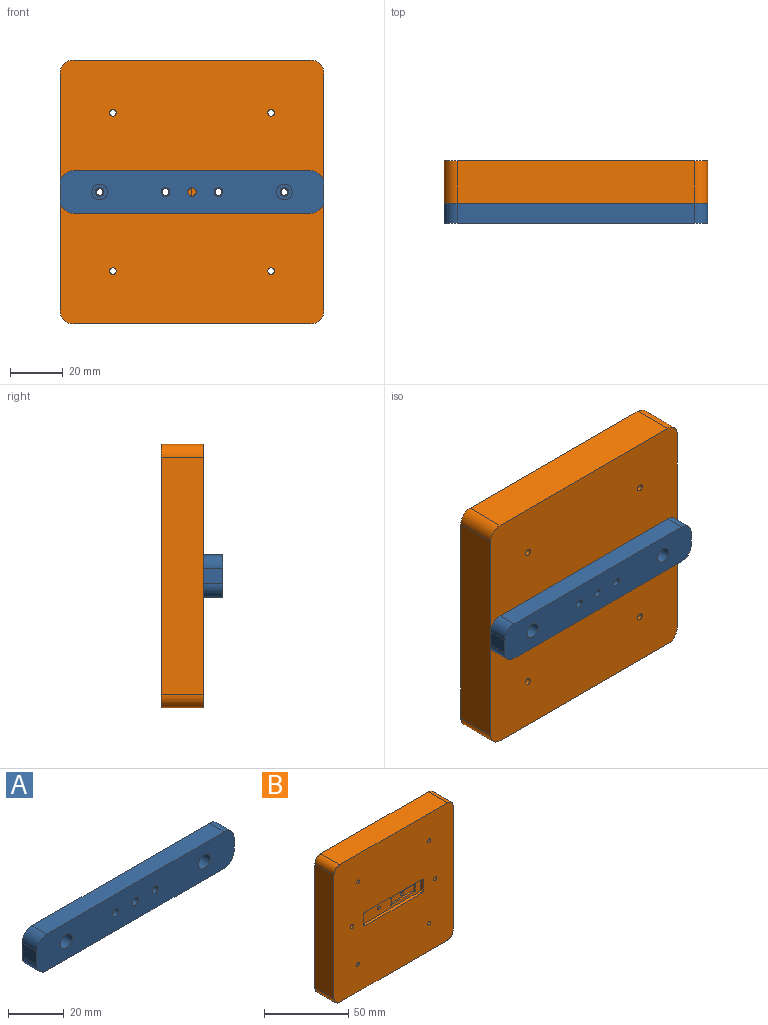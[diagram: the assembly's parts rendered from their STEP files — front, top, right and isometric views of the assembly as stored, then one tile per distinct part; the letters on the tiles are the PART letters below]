
ASSEMBLY  parts=2 mates=1
PART A: 40 faces, bbox 100x7.5x16 mm
  f0: cylinder r=1.6mm len=7mm, axis (0,-1,0), area 65mm2, adj f3,f18,f38
  f1: plane 90x7.5mm, normal (0,0,-1), area 660.3mm2, adj f3,f4,f32,f33,f34,f37,f38
  f2: cylinder r=1.6mm len=5.9mm, axis (0,-1,0), area 53.9mm2, adj f3,f27,f32
  f3: plane 100x16mm, normal (0,-1,0), area 1497.9mm2, adj f0,f1,f2,f5,f6,f7,f10,f12
  f4: plane 100x16mm, normal (0,1,0), area 1064.4mm2, adj f1,f5,f6,f7,f8,f9,f14,f15
  f5: plane 7.5x6mm, normal (1,0,0), area 45mm2, adj f3,f4,f34,f35
  f6: plane 90x7.5mm, normal (0,0,1), area 675mm2, adj f3,f4,f35,f36
  f7: plane 7.5x6mm, normal (-1,0,0), area 45mm2, adj f3,f4,f36,f37
  f8: cylinder r=1.6mm len=3.2mm, axis (0,-1,0), area 31.2mm2, adj f4,f13
  f9: cylinder r=1.6mm len=3.2mm, axis (0,-1,0), area 31.2mm2, adj f4,f11
  f10: cylinder r=3mm len=6mm, axis (0,-1,0), area 82.9mm2, adj f3,f11
  f11: plane 6x6mm, normal (0,-1,0), area 20.2mm2, adj f9,f10
  f12: cylinder r=3mm len=6mm, axis (0,-1,0), area 82.9mm2, adj f3,f13
  f13: plane 6x6mm, normal (0,-1,0), area 20.2mm2, adj f8,f12
  f14: plane 7x0.5mm, normal (1,0,0), area 3.5mm2, adj f4,f18,f28,f31
  f15: plane 47x0.5mm, normal (0,0,-1), area 23.5mm2, adj f4,f18,f28,f29
  f16: plane 7x0.5mm, normal (-1,0,0), area 3.5mm2, adj f4,f18,f29,f30
  f17: plane 47x0.5mm, normal (0,0,1), area 23.5mm2, adj f4,f18,f30,f31
  f18: plane 50x10mm, normal (0,1,0), area 382.6mm2, adj f0,f14,f15,f16,f17,f19,f20,f21
  f19: plane 19.2x1.1mm, normal (0,0,1), area 21.1mm2, adj f18,f20,f26,f27
  f20: cylinder r=0.5mm len=1.1mm, axis (0,1,0), area 2.6mm2, adj f18,f19,f21,f27
  f21: plane 4.2x1.1mm, normal (1,0,0), area 4.6mm2, adj f18,f20,f22,f27
  f22: cylinder r=0.5mm len=1.1mm, axis (0,1,0), area 2.6mm2, adj f18,f21,f23,f27
  f23: plane 19.2x1.1mm, normal (0,0,-1), area 21.1mm2, adj f18,f22,f24,f27
  f24: cylinder r=0.5mm len=1.1mm, axis (0,1,0), area 2.6mm2, adj f18,f23,f25,f27
  f25: plane 4.2x1.1mm, normal (-1,0,0), area 4.6mm2, adj f18,f24,f26,f27
  f26: cylinder r=0.5mm len=1.1mm, axis (0,1,0), area 2.6mm2, adj f18,f19,f25,f27
  f27: plane 21.2x6.2mm, normal (0,1,0), area 91.3mm2, adj f2,f19,f20,f21,f22,f23,f24,f25
  f28: cylinder r=1.5mm len=1.5mm, axis (0,-1,0), area 1.2mm2, adj f4,f14,f15,f18
  f29: cylinder r=1.5mm len=1.5mm, axis (0,1,0), area 1.2mm2, adj f4,f15,f16,f18
  f30: cylinder r=1.5mm len=1.5mm, axis (0,-1,0), area 1.2mm2, adj f4,f16,f17,f18
  f31: cylinder r=1.5mm len=1.5mm, axis (0,1,0), area 1.2mm2, adj f4,f14,f17,f18
  f32: cylinder r=1.25mm len=7mm, axis (0,0,-1), area 52.5mm2, adj f1,f2
  f33: cylinder r=1.25mm len=7mm, axis (0,0,-1), area 52.5mm2, adj f1,f39
  f34: cylinder r=5mm len=7.5mm, axis (0,1,0), area 58.9mm2, adj f1,f3,f4,f5
  f35: cylinder r=5mm len=7.5mm, axis (0,-1,0), area 58.9mm2, adj f3,f4,f5,f6
  f36: cylinder r=5mm len=7.5mm, axis (0,1,0), area 58.9mm2, adj f3,f4,f6,f7
  f37: cylinder r=5mm len=7.5mm, axis (0,-1,0), area 58.9mm2, adj f1,f3,f4,f7
  f38: cylinder r=1.25mm len=7mm, axis (0,0,-1), area 52.5mm2, adj f0,f1
  f39: cylinder r=1.6mm len=5.9mm, axis (0,-1,0), area 53.9mm2, adj f3,f27,f33
PART B: 49 faces, bbox 100x16x100 mm
  f0: plane 50x10mm, normal (0,-1,0), area 385.4mm2, adj f12,f13,f14,f15,f34,f35,f36,f37
  f1: plane 100x100mm, normal (0,-1,0), area 9451mm2, adj f3,f4,f5,f6,f12,f13,f14,f15
  f2: plane 100x100mm, normal (0,1,0), area 8151mm2, adj f3,f4,f5,f6,f7,f8,f9,f10
  f3: plane 90x16mm, normal (1,0,0), area 1440mm2, adj f1,f2,f26,f29
  f4: plane 90x16mm, normal (0,0,1), area 1440mm2, adj f1,f2,f26,f27
  f5: plane 90x16mm, normal (-1,0,0), area 1440mm2, adj f1,f2,f27,f28
  f6: plane 90x16mm, normal (0,0,-1), area 1440mm2, adj f1,f2,f28,f29
  f7: plane 27x5mm, normal (-1,0,0), area 135mm2, adj f2,f11,f30,f33
  f8: plane 57x5mm, normal (0,0,1), area 285mm2, adj f2,f11,f30,f31
  f9: plane 27x5mm, normal (1,0,0), area 135mm2, adj f2,f11,f31,f32
  f10: plane 57x5mm, normal (0,0,-1), area 285mm2, adj f2,f11,f32,f33
  f11: plane 60x30mm, normal (0,1,0), area 1757.2mm2, adj f7,f8,f9,f10,f16,f18,f30,f31
  f12: plane 7x2mm, normal (-1,0,0), area 14mm2, adj f0,f1,f34,f37
  f13: plane 47x2mm, normal (0,0,-1), area 94mm2, adj f0,f1,f34,f35
  f14: plane 7x2mm, normal (1,0,0), area 14mm2, adj f0,f1,f35,f36
  f15: plane 47x2mm, normal (0,0,1), area 94mm2, adj f0,f1,f36,f37
  f16: cylinder r=2.55mm len=6.4mm, axis (0,1,0), area 102.5mm2, adj f11,f17
  f17: plane 5.1x5.1mm, normal (0,1,0), area 15.1mm2, adj f16,f39
  f18: cylinder r=2.55mm len=7.5mm, axis (0,1,0), area 120.2mm2, adj f11,f19
  f19: plane 5.1x5.1mm, normal (0,1,0), area 15.1mm2, adj f18,f38
  f20: cylinder r=1.25mm len=16mm, axis (0,-1,0), area 125.7mm2, adj f1,f2
  f21: cylinder r=1.25mm len=16mm, axis (0,-1,0), area 125.7mm2, adj f1,f2
  f22: cylinder r=1.25mm len=16mm, axis (0,-1,0), area 125.7mm2, adj f1,f2
  f23: cylinder r=1.25mm len=16mm, axis (0,-1,0), area 125.7mm2, adj f1,f2
  f24: cylinder r=1.25mm len=16mm, axis (0,-1,0), area 125.7mm2, adj f1,f2
  f25: cylinder r=1.25mm len=16mm, axis (0,-1,0), area 125.7mm2, adj f1,f2
  f26: cylinder r=5mm len=16mm, axis (0,1,0), area 125.7mm2, adj f1,f2,f3,f4
  f27: cylinder r=5mm len=16mm, axis (0,-1,0), area 125.7mm2, adj f1,f2,f4,f5
  f28: cylinder r=5mm len=16mm, axis (0,1,0), area 125.7mm2, adj f1,f2,f5,f6
  f29: cylinder r=5mm len=16mm, axis (0,-1,0), area 125.7mm2, adj f1,f2,f3,f6
  f30: cylinder r=1.5mm len=5mm, axis (0,-1,0), area 11.8mm2, adj f2,f7,f8,f11
  f31: cylinder r=1.5mm len=5mm, axis (0,1,0), area 11.8mm2, adj f2,f8,f9,f11
  f32: cylinder r=1.5mm len=5mm, axis (0,-1,0), area 11.8mm2, adj f2,f9,f10,f11
  f33: cylinder r=1.5mm len=5mm, axis (0,1,0), area 11.8mm2, adj f2,f7,f10,f11
  f34: cylinder r=1.5mm len=2mm, axis (0,1,0), area 4.7mm2, adj f0,f1,f12,f13
  f35: cylinder r=1.5mm len=2mm, axis (0,-1,0), area 4.7mm2, adj f0,f1,f13,f14
  f36: cylinder r=1.5mm len=2mm, axis (0,1,0), area 4.7mm2, adj f0,f1,f14,f15
  f37: cylinder r=1.5mm len=2mm, axis (0,-1,0), area 4.7mm2, adj f0,f1,f12,f15
  f38: cylinder r=1.3mm len=2.6mm, axis (0,-1,0), area 12.3mm2, adj f0,f19
  f39: cylinder r=1.3mm len=2.6mm, axis (0,-1,0), area 12.3mm2, adj f17,f48
  f40: plane 4.2x1.1mm, normal (-1,0,0), area 4.6mm2, adj f0,f41,f47,f48
  f41: cylinder r=0.5mm len=1.1mm, axis (0,-1,0), area 2.6mm2, adj f0,f40,f42,f48
  f42: plane 19.2x1.1mm, normal (0,0,-1), area 21.1mm2, adj f0,f41,f43,f48
  f43: cylinder r=0.5mm len=1.1mm, axis (0,-1,0), area 2.6mm2, adj f0,f42,f44,f48
  f44: plane 4.2x1.1mm, normal (1,0,0), area 4.6mm2, adj f0,f43,f45,f48
  f45: cylinder r=0.5mm len=1.1mm, axis (0,-1,0), area 2.6mm2, adj f0,f44,f46,f48
  f46: plane 19.2x1.1mm, normal (0,0,1), area 21.1mm2, adj f0,f45,f47,f48
  f47: cylinder r=0.5mm len=1.1mm, axis (0,-1,0), area 2.6mm2, adj f0,f40,f46,f48
  f48: plane 21.2x6.2mm, normal (0,-1,0), area 102.1mm2, adj f39,f40,f41,f42,f43,f44,f45,f46
PLACE A rot(axis=(1,0,0),0deg) t=(-16.82,-18.87,4.64)mm
PLACE B t=(-16.82,-2.87,4.64)mm
MATE fastened A.f9 <-> B.f20  axis (0,1,0) through (18.18,-18.87,4.64)mm
